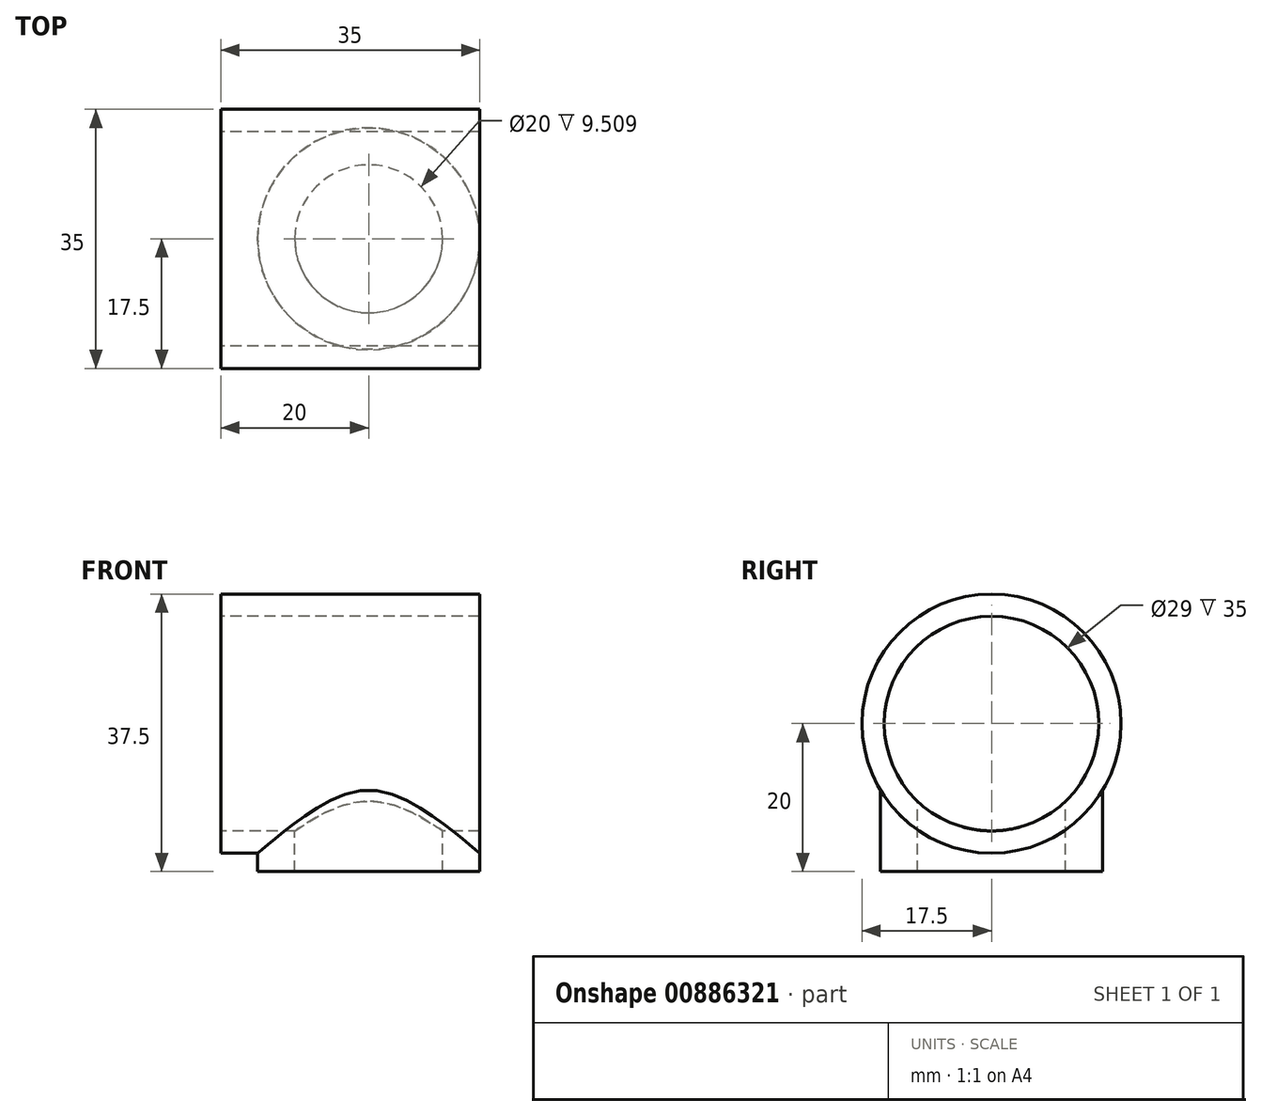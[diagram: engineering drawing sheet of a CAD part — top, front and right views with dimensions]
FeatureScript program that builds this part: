
annotation { "Feature Type Name" : "Feature", "Feature Type Description" : "" }
export const myFeature = defineFeature(function(context is Context, id is Id, definition is map)
    precondition{}
    {
        {
            var Q0;
            Q0=qCreatedBy(makeId("Right.planeOp"),FACE);
            var sketch = newSketch(context, id + "F0", { "sketchPlane" : qUnion([Q0])});
            skCircle(sketch, "E0", {"center": v(0, 0) * mm, "radius": 14.5 * mm});
            skCircle(sketch, "E1", {"center": v(0, 0) * mm, "radius": 17.5 * mm});
            skSolve(sketch);
        }
        {
            var Q0;
            Q0 = qSketchRegion(id + "F0", true);
            extrude(context, id + "F1", {"entities" : qUnion([Q0]), "depth" : 50 * mm, "offsetDistance" : 25 * mm});
        }
        {
            var Q0;
            Q0=qCreatedBy(makeId("Top.planeOp"),FACE);
            var sketch = newSketch(context, id + "F2", { "sketchPlane" : qUnion([Q0])});
            skCircle(sketch, "E2", {"center": v(20, 0) * mm, "radius": 10 * mm});
            skLineSegment(sketch, "E3", {"start": v(0, 0) * mm, "end": v(20, 0) * mm, "construction": true});
            skSolve(sketch);
        }
        {
            var Q0;
            Q0=makeQuery(id+"F2.imprint","IMPRINT",FACE,{"disambiguationData":[TD([[makeQuery(id+"F2.imprint","IMPRINT",EDGE,{"derivedFrom":sQuery(id+"F2.wireOp",EDGE,"E2")}),1.0]])]});
            extrude(context, id + "F3", {"entities" : qUnion([Q0]), "operationType" : NewBodyOperationType.REMOVE, "oppositeDirection" : true, "depth" : 25 * mm, "offsetDistance" : 25 * mm});
        }
        {
            var Q0;
            Q0=qCreatedBy(makeId("Top.planeOp"),FACE);
            cPlane(context, id + "F4", {"entities" : qUnion([Q0]), "cplaneType" : CPlaneType.OFFSET, "offset" : 20 * mm, "oppositeDirection" : true, "width" : 150 * mm, "height" : 150 * mm});
        }
        {
            var Q0;
            Q0=qCreatedBy(id+"F4.planeOp",FACE);
            var sketch = newSketch(context, id + "F5", { "sketchPlane" : qUnion([Q0])});
            skCircle(sketch, "E4", {"center": v(20, 0) * mm, "radius": 10 * mm});
            skCircle(sketch, "E5", {"center": v(20, 0) * mm, "radius": 15 * mm});
            skSolve(sketch);
        }
        {
            var Q0;
            Q0=makeQuery(id+"F5.imprint","IMPRINT",FACE,{"disambiguationData":[TD([[makeQuery(id+"F5.imprint","IMPRINT",EDGE,{"derivedFrom":sQuery(id+"F5.wireOp",EDGE,"E4")}),-1.0]])]});
            extrude(context, id + "F6", {"entities" : qUnion([Q0]), "operationType" : NewBodyOperationType.ADD, "endBound" : BoundingType.UP_TO_NEXT, "depth" : 25 * mm, "offsetDistance" : 25 * mm});
        }
        {
            var Q0;
            Q0=makeQuery(id+"F1.opExtrude","CAP_FACE",FACE,{"disambiguationData":[OSD([sQuery(id+"F0.wireOp",EDGE,"E0"),sQuery(id+"F0.wireOp",EDGE,"E1")])],"isStart":false});
            var sketch = newSketch(context, id + "F7", { "sketchPlane" : qUnion([Q0])});
            skCircle(sketch, "E6", {"center": v(0, 0) * mm, "radius": 37.44 * mm});
            skSolve(sketch);
        }
        {
            var Q0;
            Q0 = qSketchRegion(id + "F7", true);
            extrude(context, id + "F8", {"entities" : qUnion([Q0]), "operationType" : NewBodyOperationType.REMOVE, "oppositeDirection" : true, "depth" : 15 * mm, "offsetDistance" : 25 * mm});
        }
    });
